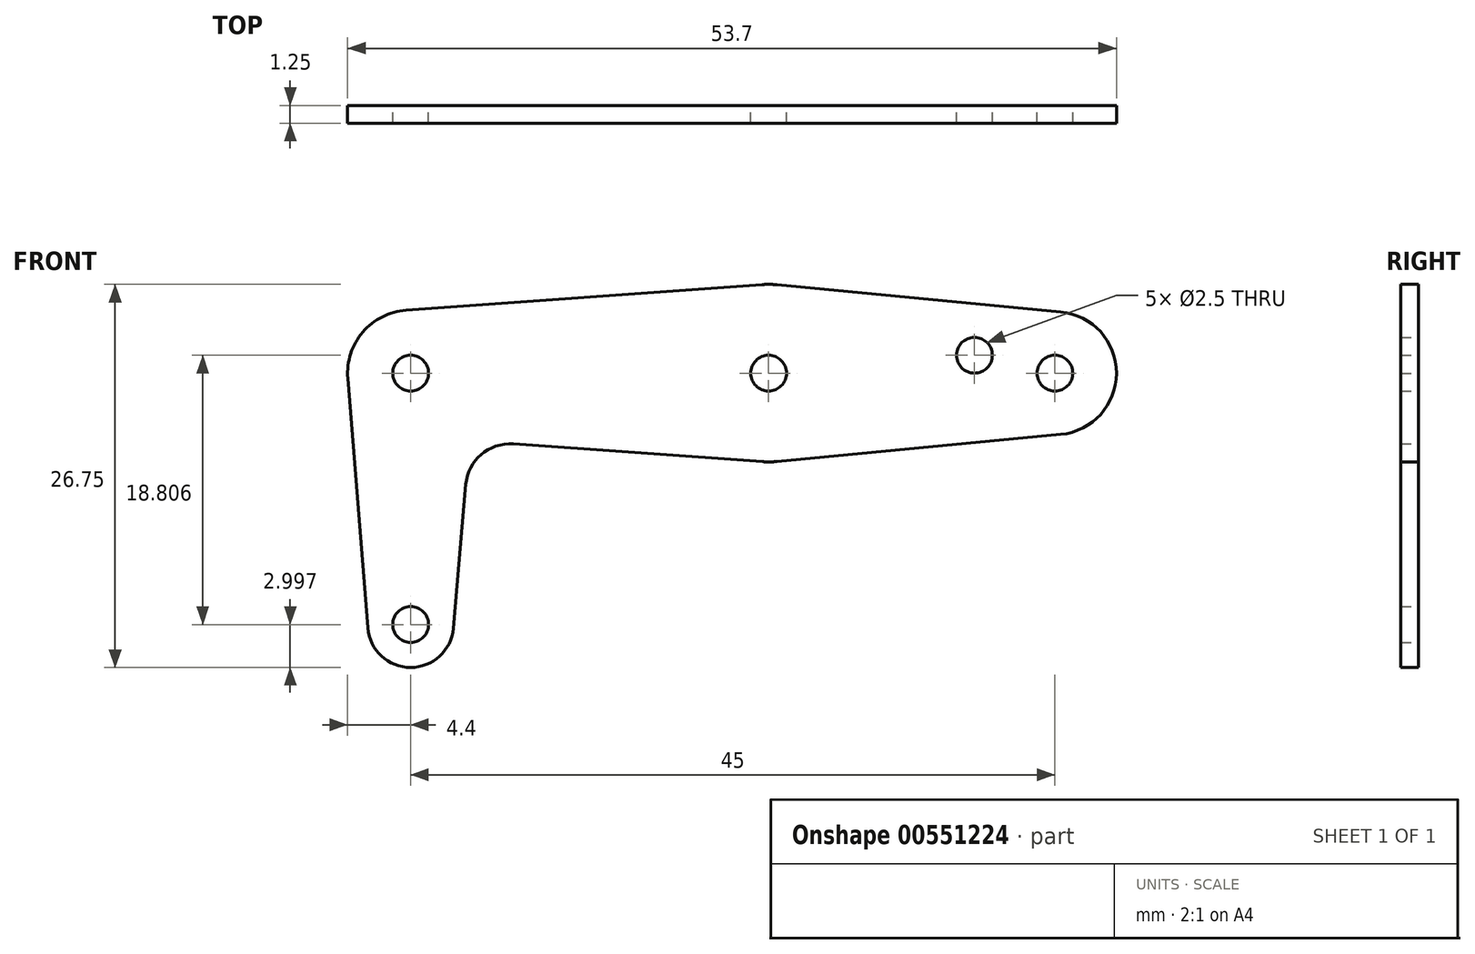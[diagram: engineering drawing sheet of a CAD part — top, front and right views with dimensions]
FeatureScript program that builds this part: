
annotation { "Feature Type Name" : "Feature", "Feature Type Description" : "" }
export const myFeature = defineFeature(function(context is Context, id is Id, definition is map)
    precondition{}
    {
        {
            var Q0;
            Q0=qCreatedBy(makeId("Front.planeOp"),FACE);
            var sketch = newSketch(context, id + "F0", { "sketchPlane" : qUnion([Q0])});
            skArc(sketch, "E0", {"start": v(-0.32, 14.88) * mm, "mid": v(-3.34, 13.36) * mm, "end": v(-4.39, 10.14) * mm});
            skArc(sketch, "E1", {"start": v(24.56, 4.3) * mm, "mid": v(25.08, 4.3) * mm, "end": v(25.59, 4.32) * mm});
            skArc(sketch, "E2", {"start": v(45.4, 6.21) * mm, "mid": v(49.3, 10.5) * mm, "end": v(45.4, 14.77) * mm});
            skArc(sketch, "E3", {"start": v(3.85, 2.72) * mm, "mid": v(4.93, 4.8) * mm, "end": v(7.16, 5.55) * mm});
            skLineSegment(sketch, "E4", {"start": v(-0.32, 14.88) * mm, "end": v(24.55, 16.68) * mm});
            skLineSegment(sketch, "E5", {"start": v(7.16, 5.55) * mm, "end": v(24.56, 4.3) * mm});
            skLineSegment(sketch, "E6", {"start": v(25.59, 4.32) * mm, "end": v(45.4, 6.21) * mm});
            skArc(sketch, "E7", {"start": v(-3, -7.3) * mm, "mid": v(0, -10.06) * mm, "end": v(2.99, -7.32) * mm});
            skLineSegment(sketch, "E8", {"start": v(-4.39, 10.14) * mm, "end": v(-3, -7.3) * mm});
            skLineSegment(sketch, "E9", {"start": v(3.85, 2.72) * mm, "end": v(2.99, -7.32) * mm});
            skCircle(sketch, "E10", {"center": v(39.38, 11.74) * mm, "radius": 1.25 * mm});
            skCircle(sketch, "E11", {"center": v(25, 10.5) * mm, "radius": 1.25 * mm});
            skCircle(sketch, "E12", {"center": v(0, 10.5) * mm, "radius": 1.25 * mm});
            skCircle(sketch, "E13", {"center": v(0, -7.06) * mm, "radius": 1.25 * mm});
            skCircle(sketch, "E14", {"center": v(45, 10.5) * mm, "radius": 1.25 * mm});
            skLineSegment(sketch, "E15", {"start": v(25.59, 16.66) * mm, "end": v(45.4, 14.77) * mm});
            skArc(sketch, "E16.trimOffspring", {"start": v(25.59, 16.66) * mm, "mid": v(25.07, 16.7) * mm, "end": v(24.55, 16.68) * mm});
            skSolve(sketch);
        }
        {
            var Q0;
            Q0=qSketchRegion(id+"F0",true);
            extrude(context, id + "F1", {"entities" : qUnion([Q0]), "depth" : 1.25 * mm, "offsetDistance" : 25 * mm});
        }
    });
